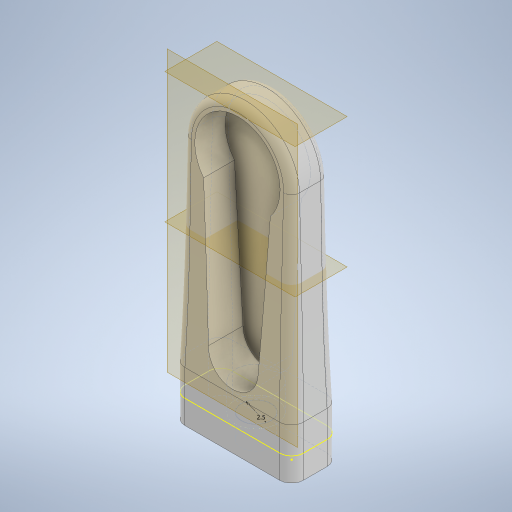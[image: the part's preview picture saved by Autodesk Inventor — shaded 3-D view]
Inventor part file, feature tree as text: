
AUTODESK INVENTOR PART (.ipt)
format: ipt  version: 2023.1 (Build 271208000, 208)  size: 488,448 bytes
history: native  units: mm
features: sketch x6, plane x3, extrude x3, fillet x3, projected_geometry x2, loft x1
ambient origin geometry x8: Origin, YZ Plane, XZ Plane, XY Plane, X Axis, Y Axis, Z Axis, Center Point
bodies: Body1 (feature_tree)
feature tree (18):
  sketch  "Sketch6"  dims[d23=10.0mm d24=4.0mm]
  plane  "Work Plane4"
  loft  "Loft3"
  extrude  "Extrusion2"  Depth=10.0mm
  fillet  "Fillet1"  Radius=4.0mm
  fillet  "Fillet2"  Radius=0.3mm
  fillet  "Fillet3"  Radius=10.0mm
  plane  "Work Plane5"
  extrude  "Extrusion3"  Depth=0.5mm
  sketch  "Sketch11"  dims[d39=10.0mm d40=21.0mm d41=4.5mm d42=7.0mm d43=19.5mm d48=4.0mm d51=4.0mm d52=16.318829mm d53=15.097098mm d54=0.1mm d55=3.0mm d56=0.0mm d57=4.566mm d58=1.0mm d59=1.0mm d60=0.6mm d61=5.0mm d62=1.0mm d63=1.0mm d64=0.6mm d65=5.0mm d66=90.0deg d67=3.5mm d68=2.25mm d69=0.0mm d70=2.5mm d71=2.0mm d72=0.0mm d9=0.5mm d10=0.872665mm d11=0.5mm d12=0.872665mm]
  extrude  "Extrusion4"  TaperAngle=0.0deg  [1 undecoded]
  plane  "Work Plane3"
  sketch  "Sketch7"  dims[d25=10.0mm d26=11.0mm d27=10.0mm d28=4.0mm d29=0.3mm d30=10.0mm]
  sketch  "Sketch8"  dims[d31=4.0mm d32=0.5mm]
  sketch  "Sketch9"  dims[d33=0.0mm d34=90.0deg d35=0.0mm d36=90.0deg]
  sketch  "Sketch10"  dims[d37=0.0mm d38=90.0deg]
  projected_geometry  "Projected Loop1"
  projected_geometry  "Projected Loop2"
note: 1 required parameter value undecoded (feature->parameter linkage not recoverable at this tier; creation-order binding heuristic only, values carry confidence <= 0.55)
